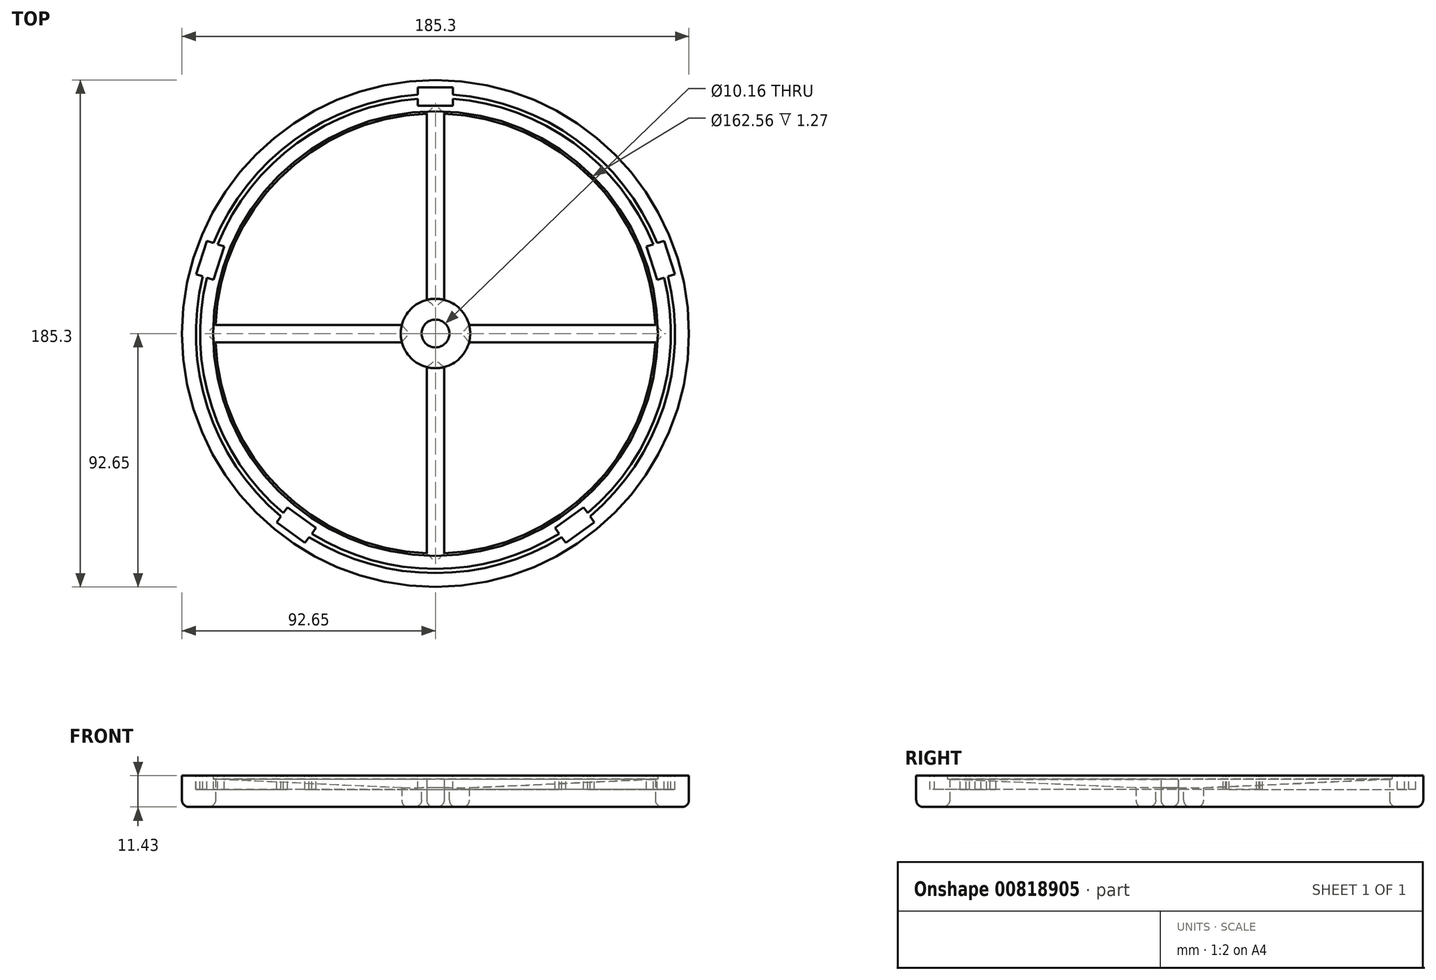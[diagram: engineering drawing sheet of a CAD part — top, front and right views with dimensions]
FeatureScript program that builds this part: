
annotation { "Feature Type Name" : "Feature", "Feature Type Description" : "" }
export const myFeature = defineFeature(function(context is Context, id is Id, definition is map)
    precondition{}
    {
        {
            var Q0;
            Q0=qCreatedBy(makeId("Front.planeOp"),FACE);
            var sketch = newSketch(context, id + "F0", { "sketchPlane" : qUnion([Q0])});
            skLineSegment(sketch, "E0", {"start": v(0, 91.39) * mm, "end": v(0, -94.44) * mm, "construction": true});
            skLineSegment(sketch, "E1", {"start": v(5.08, 0) * mm, "end": v(5.08, -10.16) * mm});
            skLineSegment(sketch, "E2", {"start": v(5.08, -10.16) * mm, "end": v(92.65, -10.16) * mm});
            skLineSegment(sketch, "E3", {"start": v(5.08, 0) * mm, "end": v(80.95, 0) * mm});
            skLineSegment(sketch, "E4.top", {"start": v(86.03, 1.27) * mm, "end": v(80.95, 1.27) * mm});
            skLineSegment(sketch, "E4.left", {"start": v(86.03, -3.8) * mm, "end": v(86.03, 1.27) * mm});
            skLineSegment(sketch, "E4.right", {"start": v(80.95, 0) * mm, "end": v(80.95, 1.27) * mm});
            skLineSegment(sketch, "E5.top", {"start": v(87.57, 1.27) * mm, "end": v(92.65, 1.27) * mm});
            skLineSegment(sketch, "E5.left", {"start": v(87.57, -3.8) * mm, "end": v(87.57, 1.27) * mm});
            skLineSegment(sketch, "E5.right", {"start": v(92.65, -10.16) * mm, "end": v(92.65, 1.27) * mm});
            skLineSegment(sketch, "E6", {"start": v(86.03, -3.8) * mm, "end": v(87.57, -3.8) * mm});
            skSolve(sketch);
        }
        {
            var Q0;
            Q0=qSketchRegion(id+"F0",true);
            var Q1;
            Q1=sQuery(id+"F0.wireOp",EDGE,"E0");
            revolve(context, id + "F1", {"surfaceOperationType" : NewSurfaceOperationType.NEW, "entities" : qUnion([Q0]), "axis" : qUnion([Q1]), "revolveType" : RevolveType.FULL});
        }
        {
            var Q0;
            Q0=makeQuery(id+"F1.opRevolve","SWEPT_FACE",FACE,{"disambiguationData":[OSD([sQuery(id+"F0.wireOp",EDGE,"E2")])]});
            var sketch = newSketch(context, id + "F2", { "sketchPlane" : qUnion([Q0])});
            skArc(sketch, "E7", {"start": v(-3.18, 80.38) * mm, "mid": v(-56.88, 56.88) * mm, "end": v(-80.38, 3.18) * mm});
            skLineSegment(sketch, "E8", {"start": v(0, 14.6) * mm, "end": v(0, 80.44) * mm, "construction": true});
            skLineSegment(sketch, "E9", {"start": v(14.6, 0) * mm, "end": v(80.44, 0) * mm, "construction": true});
            skLineSegment(sketch, "E10", {"start": v(0, -14.6) * mm, "end": v(0, -80.44) * mm, "construction": true});
            skLineSegment(sketch, "E11", {"start": v(-14.6, 0) * mm, "end": v(-80.44, 0) * mm, "construction": true});
            skArc(sketch, "E12.trimOffspring", {"start": v(-80.38, -3.18) * mm, "mid": v(-56.88, -56.88) * mm, "end": v(-3.18, -80.38) * mm});
            skArc(sketch, "E13.trimOffspring", {"start": v(80.38, 3.18) * mm, "mid": v(56.88, 56.88) * mm, "end": v(3.17, 80.38) * mm});
            skLineSegment(sketch, "E14.bottom", {"start": v(-80.38, 3.18) * mm, "end": v(-12.3, 3.18) * mm});
            skLineSegment(sketch, "E14.top", {"start": v(-80.38, -3.17) * mm, "end": v(-12.3, -3.17) * mm});
            skLineSegment(sketch, "E15.left", {"start": v(-3.18, 80.38) * mm, "end": v(-3.18, 12.3) * mm});
            skLineSegment(sketch, "E15.right", {"start": v(3.17, 80.38) * mm, "end": v(3.17, 12.3) * mm});
            skArc(sketch, "E16", {"start": v(-3.18, 12.3) * mm, "mid": v(-8.98, 8.98) * mm, "end": v(-12.3, 3.18) * mm});
            skArc(sketch, "E17.trimOffspring", {"start": v(3.18, -80.38) * mm, "mid": v(56.88, -56.88) * mm, "end": v(80.38, -3.17) * mm});
            skLineSegment(sketch, "E18.trimOffspring", {"start": v(-3.18, -12.3) * mm, "end": v(-3.18, -80.38) * mm});
            skLineSegment(sketch, "E19.trimOffspring", {"start": v(3.17, -12.3) * mm, "end": v(3.17, -80.38) * mm});
            skArc(sketch, "E20.trimOffspring", {"start": v(3.17, -12.3) * mm, "mid": v(8.98, -8.98) * mm, "end": v(12.3, -3.17) * mm});
            skArc(sketch, "E21.trimOffspring", {"start": v(-12.3, -3.17) * mm, "mid": v(-8.98, -8.98) * mm, "end": v(-3.18, -12.3) * mm});
            skArc(sketch, "E22.trimOffspring", {"start": v(12.3, 3.18) * mm, "mid": v(8.98, 8.98) * mm, "end": v(3.17, 12.3) * mm});
            skLineSegment(sketch, "E23.trimOffspring", {"start": v(12.3, -3.17) * mm, "end": v(80.38, -3.17) * mm});
            skLineSegment(sketch, "E24.trimOffspring", {"start": v(12.3, 3.18) * mm, "end": v(80.38, 3.18) * mm});
            skPoint(sketch, "E14.right.end.orphan", {"position": v(83.26, -3.17) * mm});
            skPoint(sketch, "E25.orphan", {"position": v(-83.42, 3.18) * mm});
            skPoint(sketch, "E26.orphan", {"position": v(-3.18, 83.79) * mm});
            skSolve(sketch);
        }
        {
            var Q0;
            Q0=qSketchRegion(id+"F2",true);
            var Q1;
            Q1=makeQuery(id+"F1.opRevolve","SWEPT_FACE",FACE,{"disambiguationData":[OSD([sQuery(id+"F0.wireOp",EDGE,"E3")])]});
            extrude(context, id + "F3", {"entities" : qUnion([Q0, Q1]), "operationType" : NewBodyOperationType.REMOVE, "oppositeDirection" : true, "depth" : 25.4 * mm, "offsetDistance" : 25.4 * mm});
        }
        {
            var Q0;
            Q0=makeQuery(id+"F1.opRevolve","SWEPT_FACE",FACE,{"disambiguationData":[OSD([sQuery(id+"F0.wireOp",EDGE,"E5.top")])]});
            var sketch = newSketch(context, id + "F4", { "sketchPlane" : qUnion([Q0])});
            skLineSegment(sketch, "E27.bottom", {"start": v(-6.41, 89.93) * mm, "end": v(6.41, 89.93) * mm});
            skLineSegment(sketch, "E27.top", {"start": v(-6.41, 83.2) * mm, "end": v(6.41, 83.2) * mm});
            skLineSegment(sketch, "E27.left", {"start": v(-6.41, 89.93) * mm, "end": v(-6.41, 83.2) * mm});
            skLineSegment(sketch, "E27.right", {"start": v(6.41, 89.93) * mm, "end": v(6.41, 83.2) * mm});
            skPoint(sketch, "E28.center", {"position": v(0, 0) * mm});
            skLineSegment(sketch, "E29.1.0", {"start": v(-87.5, 21.69) * mm, "end": v(-83.55, 33.89) * mm});
            skLineSegment(sketch, "E29.1.1", {"start": v(-81.1, 19.6) * mm, "end": v(-77.14, 31.8) * mm});
            skLineSegment(sketch, "E29.1.2", {"start": v(-87.5, 21.69) * mm, "end": v(-81.1, 19.6) * mm});
            skLineSegment(sketch, "E29.1.3", {"start": v(-83.55, 33.89) * mm, "end": v(-77.14, 31.8) * mm});
            skLineSegment(sketch, "E29.2.0", {"start": v(-47.67, -76.52) * mm, "end": v(-58.05, -68.98) * mm});
            skLineSegment(sketch, "E29.2.1", {"start": v(-43.71, -71.08) * mm, "end": v(-54.1, -63.54) * mm});
            skLineSegment(sketch, "E29.2.2", {"start": v(-47.67, -76.52) * mm, "end": v(-43.71, -71.08) * mm});
            skLineSegment(sketch, "E29.2.3", {"start": v(-58.05, -68.98) * mm, "end": v(-54.1, -63.54) * mm});
            skLineSegment(sketch, "E29.3.0", {"start": v(58.05, -68.98) * mm, "end": v(47.67, -76.52) * mm});
            skLineSegment(sketch, "E29.3.1", {"start": v(54.1, -63.54) * mm, "end": v(43.71, -71.08) * mm});
            skLineSegment(sketch, "E29.3.2", {"start": v(58.05, -68.98) * mm, "end": v(54.1, -63.54) * mm});
            skLineSegment(sketch, "E29.3.3", {"start": v(47.67, -76.52) * mm, "end": v(43.71, -71.08) * mm});
            skLineSegment(sketch, "E29.4.0", {"start": v(83.55, 33.89) * mm, "end": v(87.5, 21.69) * mm});
            skLineSegment(sketch, "E29.4.1", {"start": v(77.14, 31.8) * mm, "end": v(81.1, 19.6) * mm});
            skLineSegment(sketch, "E29.4.2", {"start": v(83.55, 33.89) * mm, "end": v(77.14, 31.8) * mm});
            skLineSegment(sketch, "E29.4.3", {"start": v(87.5, 21.69) * mm, "end": v(81.1, 19.6) * mm});
            skSolve(sketch);
        }
        {
            var Q0;
            Q0=qSketchRegion(id+"F4",true);
            extrude(context, id + "F5", {"entities" : qUnion([Q0]), "operationType" : NewBodyOperationType.REMOVE, "oppositeDirection" : true, "depth" : 5.08 * mm, "offsetDistance" : 25.4 * mm});
        }
        {
            var Q0;
            Q0=makeQuery(id+"F1.opRevolve","SWEPT_BODY",BODY,{"disambiguationData":[OSD([sQuery(id+"F0.wireOp",EDGE,"E1"),sQuery(id+"F0.wireOp",EDGE,"E2"),sQuery(id+"F0.wireOp",EDGE,"E3"),sQuery(id+"F0.wireOp",EDGE,"E4.top"),sQuery(id+"F0.wireOp",EDGE,"E4.left"),sQuery(id+"F0.wireOp",EDGE,"E4.right"),sQuery(id+"F0.wireOp",EDGE,"E5.top"),sQuery(id+"F0.wireOp",EDGE,"E5.left"),sQuery(id+"F0.wireOp",EDGE,"E5.right"),sQuery(id+"F0.wireOp",EDGE,"E6")])]});
            transform(context, id + "F6", {"entities" : qUnion([Q0]), "transformType" : TransformType.TRANSLATION_3D, "dx" : 0 * mm, "dy" : 0 * mm, "dz" : 0 * mm, "makeCopy" : true});
        }
        {
            var Q0;
            Q0=makeQuery(id+"F6.opPattern","COPY",BODY,{"derivedFrom":makeQuery(id+"F1.opRevolve","SWEPT_BODY",BODY,{"disambiguationData":[OSD([sQuery(id+"F0.wireOp",EDGE,"E1"),sQuery(id+"F0.wireOp",EDGE,"E2"),sQuery(id+"F0.wireOp",EDGE,"E3"),sQuery(id+"F0.wireOp",EDGE,"E4.top"),sQuery(id+"F0.wireOp",EDGE,"E4.left"),sQuery(id+"F0.wireOp",EDGE,"E4.right"),sQuery(id+"F0.wireOp",EDGE,"E5.top"),sQuery(id+"F0.wireOp",EDGE,"E5.left"),sQuery(id+"F0.wireOp",EDGE,"E5.right"),sQuery(id+"F0.wireOp",EDGE,"E6")])]}),"instanceName":"1"});
            deleteBodies(context, id + "F7", {"entities" : qUnion([Q0])});
        }
        {
            var Q0;
            Q0=qCreatedBy(makeId("Front.planeOp"),FACE);
            var sketch = newSketch(context, id + "F8", { "sketchPlane" : qUnion([Q0])});
            skLineSegment(sketch, "E30", {"start": v(-12.7, -3.17) * mm, "end": v(-81.28, 0) * mm});
            skLineSegment(sketch, "E31", {"start": v(-81.28, 5.6) * mm, "end": v(-81.28, 0) * mm});
            skLineSegment(sketch, "E32", {"start": v(-81.28, 5.6) * mm, "end": v(-4.57, 5.76) * mm});
            skLineSegment(sketch, "E33", {"start": v(-3.5, -3.17) * mm, "end": v(-12.7, -3.17) * mm});
            skLineSegment(sketch, "E34", {"start": v(-4.57, 5.76) * mm, "end": v(-3.5, -3.17) * mm});
            skLineSegment(sketch, "E35", {"start": v(0, 6.5) * mm, "end": v(0, -22.52) * mm, "construction": true});
            skSolve(sketch);
        }
        {
            var Q0;
            Q0=qSketchRegion(id+"F8",true);
            var Q1;
            Q1=sQuery(id+"F8.wireOp",EDGE,"E35");
            revolve(context, id + "F9", {"operationType" : NewBodyOperationType.REMOVE, "surfaceOperationType" : NewSurfaceOperationType.NEW, "entities" : qUnion([Q0]), "axis" : qUnion([Q1]), "revolveType" : RevolveType.ONE_DIRECTION, "oppositeDirection" : true, "angle" : 360 * degree});
        }
        {
            var Q0;
            Q0=makeQuery(id+"F1.opRevolve","SWEPT_FACE",FACE,{"disambiguationData":[OSD([sQuery(id+"F0.wireOp",EDGE,"E2")])]});
            fillet(context, id + "F10", {"entities" : qUnion([Q0]), "radius" : 2.54 * mm, "tangentPropagation" : true, "allowEdgeOverflow" : false});
        }
    });
